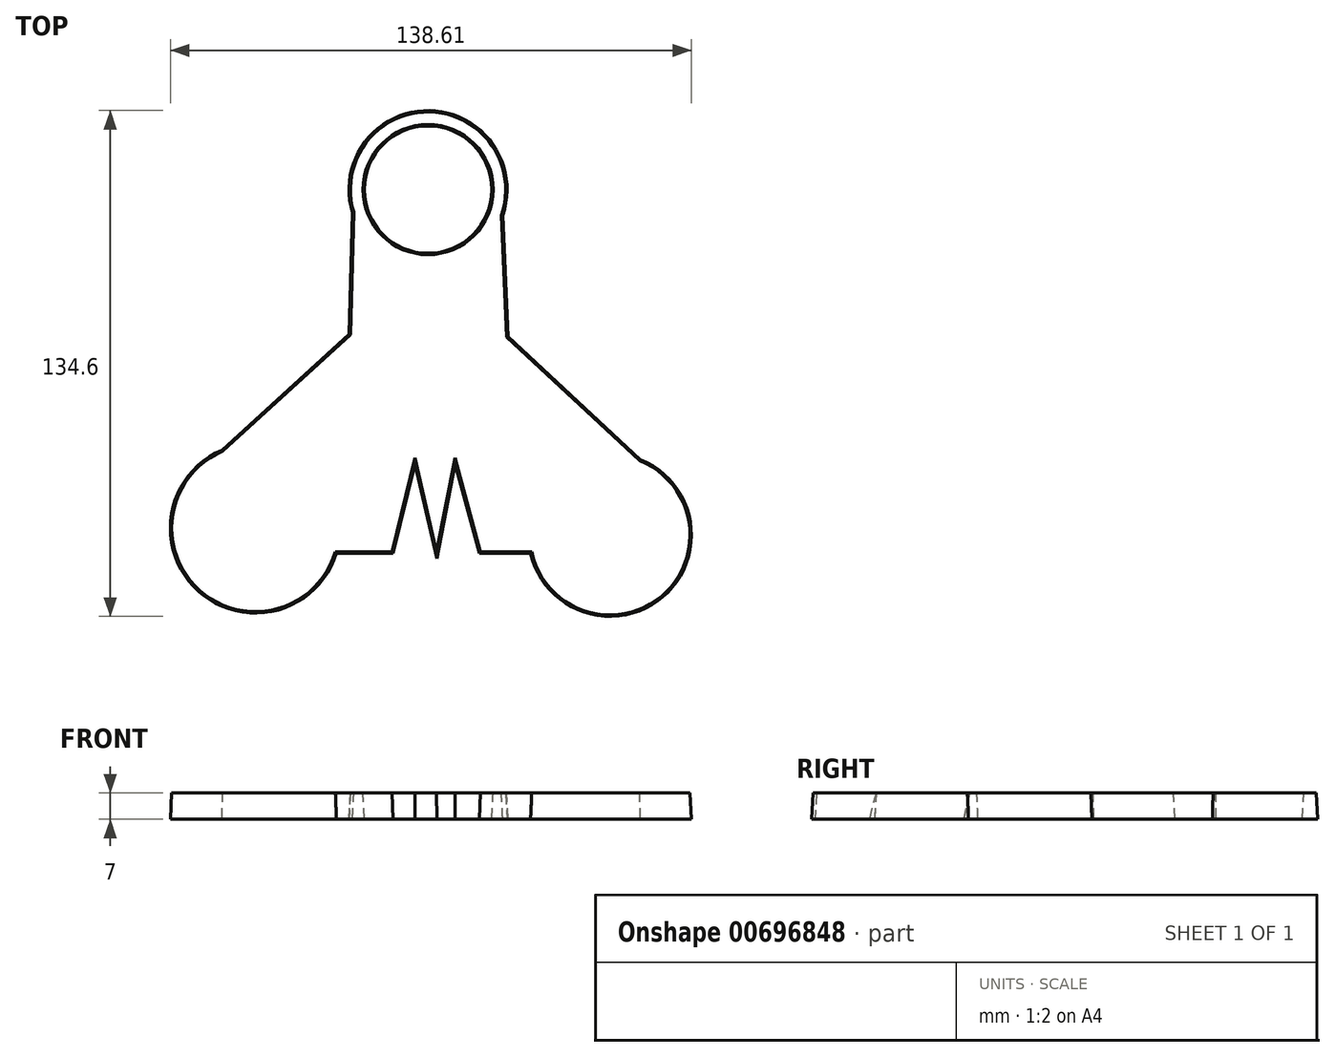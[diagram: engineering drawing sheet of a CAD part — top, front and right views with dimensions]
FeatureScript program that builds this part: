
annotation { "Feature Type Name" : "Feature", "Feature Type Description" : "" }
export const myFeature = defineFeature(function(context is Context, id is Id, definition is map)
    precondition{}
    {
        {
            var Q0;
            Q0=qCreatedBy(makeId("Top.planeOp"),FACE);
            var sketch = newSketch(context, id + "F0", { "sketchPlane" : qUnion([Q0])});
            skCircle(sketch, "E0", {"center": v(0, 0) * mm, "radius": 18.37 * mm});
            skCircle(sketch, "E1", {"center": v(0, 48.7) * mm, "radius": 17.31 * mm});
            skArc(sketch, "E2", {"start": v(19.5, 41.9) * mm, "mid": v(0.41, 69.36) * mm, "end": v(-19.76, 42.68) * mm});
            skCircle(sketch, "E3", {"center": v(-45.96, -41.38) * mm, "radius": 17.72 * mm});
            skCircle(sketch, "E4", {"center": v(48.4, -43.21) * mm, "radius": 17.26 * mm});
            skArc(sketch, "E5", {"start": v(-54.65, -20.92) * mm, "mid": v(-60.75, -57.97) * mm, "end": v(-24.64, -47.66) * mm});
            skArc(sketch, "E6", {"start": v(27.58, -47.66) * mm, "mid": v(62.13, -59.5) * mm, "end": v(56.3, -23.44) * mm});
            skLineSegment(sketch, "E7", {"start": v(-19.76, 42.68) * mm, "end": v(-20.67, 10.03) * mm});
            skLineSegment(sketch, "E8", {"start": v(-20.67, 10.03) * mm, "end": v(-54.65, -20.92) * mm});
            skLineSegment(sketch, "E9", {"start": v(19.5, 41.9) * mm, "end": v(20.93, 9.47) * mm});
            skLineSegment(sketch, "E10", {"start": v(20.93, 9.47) * mm, "end": v(56.3, -23.44) * mm});
            skLineSegment(sketch, "E11", {"start": v(-24.64, -47.66) * mm, "end": v(-9.62, -47.66) * mm});
            skLineSegment(sketch, "E12", {"start": v(-9.62, -47.66) * mm, "end": v(-3.42, -22.72) * mm});
            skLineSegment(sketch, "E13", {"start": v(-3.42, -22.72) * mm, "end": v(2.3, -47.66) * mm});
            skLineSegment(sketch, "E14", {"start": v(2.3, -47.66) * mm, "end": v(7.18, -22.72) * mm});
            skLineSegment(sketch, "E15", {"start": v(7.18, -22.72) * mm, "end": v(13.9, -47.66) * mm});
            skLineSegment(sketch, "E16", {"start": v(13.9, -47.66) * mm, "end": v(27.58, -47.66) * mm});
            skSolve(sketch);
        }
        {
            var Q0;
            Q0=makeQuery(id+"F0.imprint","IMPRINT",FACE,{"disambiguationData":[TD([[makeQuery(id+"F0.imprint","IMPRINT",EDGE,{"derivedFrom":sQuery(id+"F0.wireOp",EDGE,"E0")}),-1.0]])]});
            var Q1;
            Q1=makeQuery(id+"F0.imprint","IMPRINT",FACE,{"disambiguationData":[TD([[makeQuery(id+"F0.imprint","IMPRINT",EDGE,{"derivedFrom":sQuery(id+"F0.wireOp",EDGE,"E0")}),1.0]])]});
            var Q2;
            Q2=makeQuery(id+"F0.imprint","IMPRINT",FACE,{"disambiguationData":[TD([[makeQuery(id+"F0.imprint","IMPRINT",EDGE,{"derivedFrom":sQuery(id+"F0.wireOp",EDGE,"E4")}),1.0]])]});
            var Q3;
            Q3=makeQuery(id+"F0.imprint","IMPRINT",FACE,{"disambiguationData":[TD([[makeQuery(id+"F0.imprint","IMPRINT",EDGE,{"derivedFrom":sQuery(id+"F0.wireOp",EDGE,"E3")}),1.0]])]});
            extrude(context, id + "F1", {"entities" : qUnion([Q0, Q1, Q2, Q3]), "oppositeDirection" : true, "depth" : 7 * mm, "offsetDistance" : 25.4 * mm, "hasDraft" : true, "draftAngle" : 3 * degree});
        }
    });
